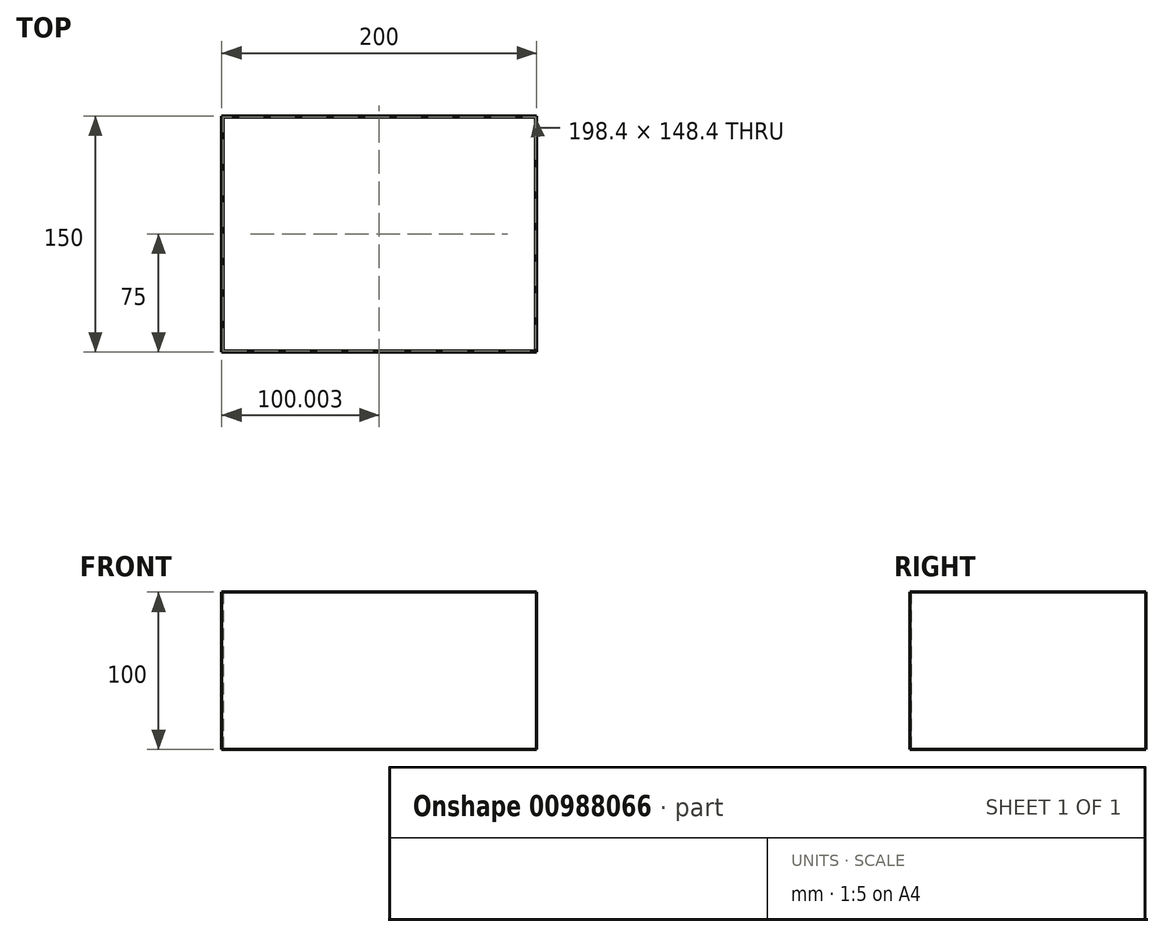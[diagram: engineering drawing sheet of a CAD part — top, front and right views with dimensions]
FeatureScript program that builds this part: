
annotation { "Feature Type Name" : "Feature", "Feature Type Description" : "" }
export const myFeature = defineFeature(function(context is Context, id is Id, definition is map)
    precondition{}
    {
        {
            var Q0;
            Q0=qCreatedBy(makeId("Top.planeOp"),FACE);
            var sketch = newSketch(context, id + "F0", { "sketchPlane" : qUnion([Q0])});
            skLineSegment(sketch, "E0.bottom", {"start": v(-99.97, 82.53) * mm, "end": v(100.03, 82.53) * mm});
            skLineSegment(sketch, "E0.top", {"start": v(-99.97, -67.47) * mm, "end": v(100.03, -67.47) * mm});
            skLineSegment(sketch, "E0.left", {"start": v(-99.97, 82.53) * mm, "end": v(-99.97, -67.47) * mm});
            skLineSegment(sketch, "E0.right", {"start": v(100.03, 82.53) * mm, "end": v(100.03, -67.47) * mm});
            skLineSegment(sketch, "E1.bottom", {"start": v(-99.17, 81.73) * mm, "end": v(99.23, 81.73) * mm});
            skLineSegment(sketch, "E1.top", {"start": v(-99.17, -66.67) * mm, "end": v(99.23, -66.67) * mm});
            skLineSegment(sketch, "E1.left", {"start": v(-99.17, 81.73) * mm, "end": v(-99.17, -66.67) * mm});
            skLineSegment(sketch, "E1.right", {"start": v(99.23, 81.73) * mm, "end": v(99.23, -66.67) * mm});
            skSolve(sketch);
        }
        {
            var Q0;
            Q0=makeQuery(id+"F0.imprint","IMPRINT",FACE,{"disambiguationData":[TD([[makeQuery(id+"F0.imprint","IMPRINT",EDGE,{"derivedFrom":sQuery(id+"F0.wireOp",EDGE,"E0.bottom")}),-1.0]])]});
            extrude(context, id + "F1", {"entities" : qUnion([Q0]), "depth" : 100 * mm, "offsetDistance" : 25 * mm});
        }
    });
